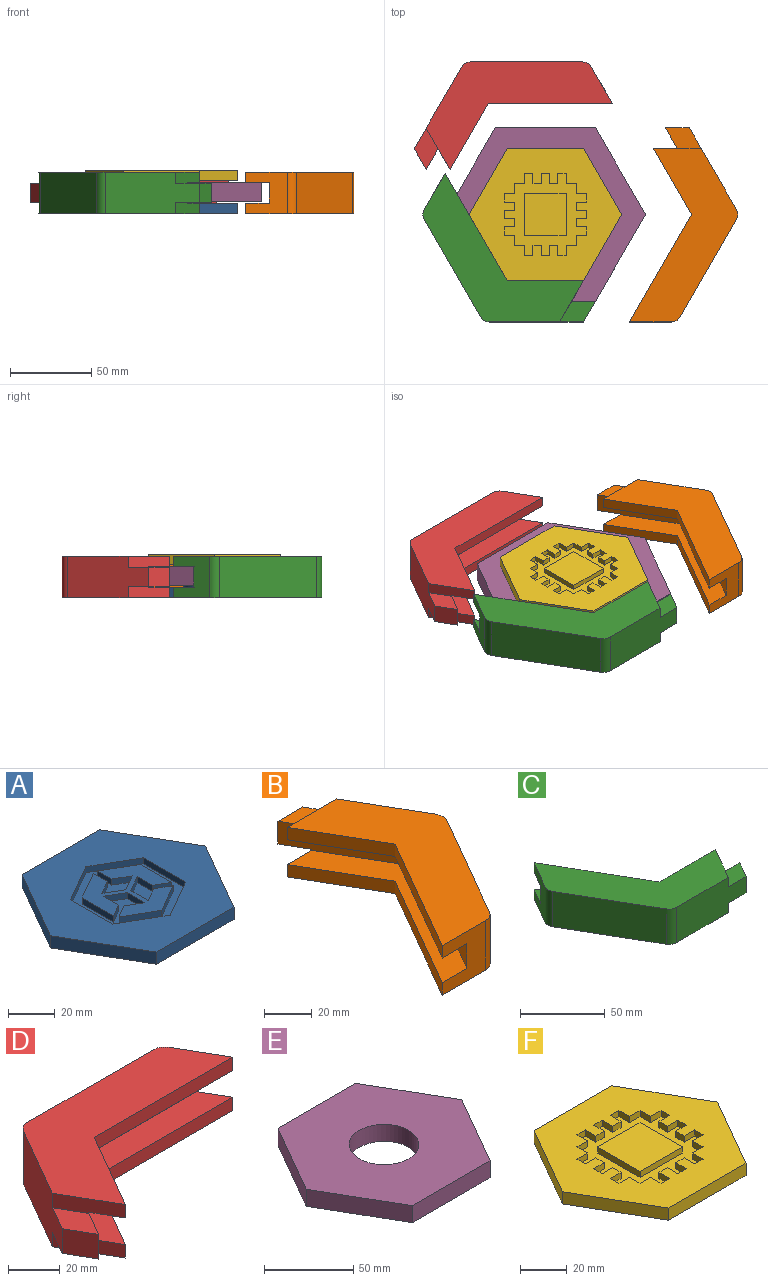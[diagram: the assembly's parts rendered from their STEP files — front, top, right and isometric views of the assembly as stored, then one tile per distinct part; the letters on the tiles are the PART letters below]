
ASSEMBLY  parts=6 mates=5
PART A: 42 faces, bbox 93.7x81.2x12.7 mm
  f0: plane 93.74x81.18mm, normal (0,0,1), area 4031.4mm2, adj f1,f2,f3,f4,f5,f6,f33,f34
  f1: plane 40.59x23.44mm, normal (-0.87,-0.5,0), area 297.6mm2, adj f0,f2,f6,f7
  f2: plane 46.87x6.35mm, normal (0,-1,0), area 297.6mm2, adj f0,f1,f3,f7
  f3: plane 40.59x23.44mm, normal (0.87,-0.5,0), area 297.6mm2, adj f0,f2,f4,f7
  f4: plane 40.59x23.44mm, normal (0.87,0.5,0), area 297.6mm2, adj f0,f3,f5,f7
  f5: plane 46.87x6.35mm, normal (0,1,0), area 297.6mm2, adj f0,f4,f6,f7
  f6: plane 40.59x23.44mm, normal (-0.87,0.5,0), area 297.6mm2, adj f0,f1,f5,f7
  f7: plane 93.74x81.18mm, normal (0,0,-1), area 4567.5mm2, adj f1,f2,f3,f4,f5,f6,f8
  f8: cylinder r=19.05mm len=38.1mm, axis (0,0,1), area 760.1mm2, adj f7,f9
  f9: plane 38.1x38.1mm, normal (0,0,-1), area 1140.1mm2, adj f8
  f10: plane 16.33x9.43mm, normal (-0.5,0.87,0), area 59.9mm2, adj f11,f39,f40,f41
  f11: plane 8.46x3.18mm, normal (1,0,0), area 26.9mm2, adj f10,f12,f40,f41
  f12: plane 7.9x4.56mm, normal (0.5,-0.87,0), area 29mm2, adj f11,f13,f40,f41
  f13: plane 9.17x5.3mm, normal (0.5,0.87,0), area 33.6mm2, adj f12,f14,f40,f41
  f14: plane 9.17x5.3mm, normal (-0.5,0.87,0), area 33.6mm2, adj f13,f15,f40,f41
  f15: plane 7.9x4.56mm, normal (-0.5,-0.87,0), area 29mm2, adj f14,f16,f40,f41
  f16: plane 8.46x3.18mm, normal (-1,0,0), area 26.9mm2, adj f15,f17,f40,f41
  f17: plane 16.33x9.43mm, normal (0.5,0.87,0), area 59.9mm2, adj f16,f18,f40,f41
  f18: plane 18.85x3.18mm, normal (1,0,0), area 59.9mm2, adj f17,f19,f40,f41
  f19: plane 7.33x4.23mm, normal (-0.5,-0.87,0), area 26.9mm2, adj f18,f20,f40,f41
  f20: plane 9.13x3.18mm, normal (-1,0,0), area 29mm2, adj f19,f21,f40,f41
  f21: plane 9.17x5.3mm, normal (0.5,-0.87,0), area 33.6mm2, adj f20,f22,f40,f41
  f22: plane 10.59x3.18mm, normal (1,0,0), area 33.6mm2, adj f21,f23,f40,f41
  f23: plane 7.9x4.56mm, normal (-0.5,0.87,0), area 29mm2, adj f22,f24,f40,f41
  f24: plane 7.33x4.23mm, normal (0.5,0.87,0), area 26.9mm2, adj f23,f25,f40,f41
  f25: plane 16.33x9.43mm, normal (0.5,-0.87,0), area 59.9mm2, adj f24,f26,f40,f41
  f26: plane 16.33x9.43mm, normal (-0.5,-0.87,0), area 59.9mm2, adj f25,f27,f40,f41
  f27: plane 7.33x4.23mm, normal (-0.5,0.87,0), area 26.9mm2, adj f26,f28,f40,f41
  f28: plane 7.9x4.56mm, normal (0.5,0.87,0), area 29mm2, adj f27,f29,f40,f41
  f29: plane 10.59x3.18mm, normal (-1,0,0), area 33.6mm2, adj f28,f30,f40,f41
  f30: plane 9.17x5.3mm, normal (-0.5,-0.87,0), area 33.6mm2, adj f29,f31,f40,f41
  f31: plane 9.13x3.18mm, normal (1,0,0), area 29mm2, adj f30,f32,f40,f41
  f32: plane 7.33x4.23mm, normal (0.5,-0.87,0), area 26.9mm2, adj f31,f39,f40,f41
  f33: plane 22x12.7mm, normal (0.5,0.87,0), area 80.6mm2, adj f0,f34,f38,f40
  f34: plane 22x12.7mm, normal (-0.5,0.87,0), area 80.6mm2, adj f0,f33,f35,f40
  f35: plane 25.4x3.18mm, normal (-1,0,0), area 80.6mm2, adj f0,f34,f36,f40
  f36: plane 22x12.7mm, normal (-0.5,-0.87,0), area 80.6mm2, adj f0,f35,f37,f40
  f37: plane 22x12.7mm, normal (0.5,-0.87,0), area 80.6mm2, adj f0,f36,f38,f40
  f38: plane 25.4x3.18mm, normal (1,0,0), area 80.6mm2, adj f0,f33,f37,f40
  f39: plane 18.85x3.18mm, normal (-1,0,0), area 59.9mm2, adj f10,f32,f40,f41
  f40: plane 50.8x43.99mm, normal (0,0,1), area 959.3mm2, adj f10,f11,f12,f13,f14,f15,f16,f17
  f41: plane 39.91x35.2mm, normal (0,0,1), area 716.8mm2, adj f10,f11,f12,f13,f14,f15,f16,f17
PART B: 20 faces, bbox 66.4x119.3x25.4 mm
  f0: plane 29.33x6.86mm, normal (0,1,0), area 193.7mm2, adj f1,f3,f5,f14,f16,f18
  f1: plane 40.59x23.44mm, normal (-0.87,-0.5,0), area 297.6mm2, adj f0,f2,f14,f18
  f2: plane 65.99x38.1mm, normal (-0.87,0.5,0), area 483.9mm2, adj f1,f9,f14,f18
  f3: plane 50.12x28.93mm, normal (0.87,0.5,0), area 1268.7mm2, adj f0,f4,f6,f12,f13,f14,f15,f16
  f4: plane 14.66x11.68mm, normal (0,1,0), area 171.3mm2, adj f3,f5,f15,f16
  f5: plane 53.29x30.77mm, normal (-0.87,-0.5,0), area 766.6mm2, adj f0,f4,f6,f15,f16,f17,f18,f19
  f6: plane 29.33x6.86mm, normal (0,1,0), area 193.7mm2, adj f3,f5,f7,f13,f15,f19
  f7: plane 40.59x23.44mm, normal (-0.87,-0.5,0), area 297.6mm2, adj f6,f8,f13,f19
  f8: plane 65.99x38.1mm, normal (-0.87,0.5,0), area 483.9mm2, adj f7,f9,f13,f19
  f9: plane 25.66x25.4mm, normal (0,-1,0), area 465.6mm2, adj f2,f8,f10,f13,f14,f17,f18,f19
  f10: cylinder r=6.35mm len=25.4mm, axis (0,0,-1), area 168.9mm2, adj f9,f11,f13,f14
  f11: plane 59.64x34.43mm, normal (0.87,-0.5,0), area 1749.2mm2, adj f10,f12,f13,f14
  f12: cylinder r=6.35mm len=25.4mm, axis (0,0,-1), area 168.9mm2, adj f3,f11,f13,f14
  f13: plane 106.58x66.45mm, normal (0,0,1), area 3121.7mm2, adj f3,f6,f7,f8,f9,f10,f11,f12
  f14: plane 106.58x66.45mm, normal (0,0,-1), area 3121.7mm2, adj f0,f1,f2,f3,f9,f10,f11,f12
  f15: plane 22x12.7mm, normal (0,0,1), area 186.2mm2, adj f3,f4,f5,f6
  f16: plane 22x12.7mm, normal (0,0,-1), area 186.2mm2, adj f0,f3,f4,f5
  f17: plane 65.99x38.1mm, normal (-0.87,0.5,0), area 967.7mm2, adj f5,f9,f18,f19
  f18: plane 106.58x52.76mm, normal (0,0,1), area 1563mm2, adj f0,f1,f2,f5,f9,f17
  f19: plane 106.58x52.76mm, normal (0,0,-1), area 1563mm2, adj f5,f6,f7,f8,f9,f17
PART C: 20 faces, bbox 106x91.4x25.4 mm
  f0: plane 25.4x14.66mm, normal (0.87,-0.5,0), area 193.7mm2, adj f1,f3,f5,f14,f16,f18
  f1: plane 46.87x6.35mm, normal (0,1,0), area 297.6mm2, adj f0,f2,f14,f18
  f2: plane 65.99x38.1mm, normal (0.87,0.5,0), area 483.9mm2, adj f1,f9,f14,f18
  f3: plane 57.87x25.4mm, normal (0,-1,0), area 1268.7mm2, adj f0,f4,f6,f12,f13,f14,f15,f16
  f4: plane 12.7x11.68mm, normal (0.87,-0.5,0), area 171.3mm2, adj f3,f5,f15,f16
  f5: plane 61.54x12.7mm, normal (0,1,0), area 766.6mm2, adj f0,f4,f6,f15,f16,f17,f18,f19
  f6: plane 25.4x14.66mm, normal (0.87,-0.5,0), area 193.7mm2, adj f3,f5,f7,f13,f15,f19
  f7: plane 46.87x6.35mm, normal (0,1,0), area 297.6mm2, adj f6,f8,f13,f19
  f8: plane 65.99x38.1mm, normal (0.87,0.5,0), area 483.9mm2, adj f7,f9,f13,f19
  f9: plane 25.4x22.23mm, normal (-0.87,0.5,0), area 465.6mm2, adj f2,f8,f10,f13,f14,f17,f18,f19
  f10: cylinder r=6.35mm len=25.4mm, axis (0,0,-1), area 168.9mm2, adj f9,f11,f13,f14
  f11: plane 59.64x34.43mm, normal (-0.87,-0.5,0), area 1749.2mm2, adj f10,f12,f13,f14
  f12: cylinder r=6.35mm len=25.4mm, axis (0,0,-1), area 168.9mm2, adj f3,f11,f13,f14
  f13: plane 98.65x91.39mm, normal (0,0,1), area 3121.7mm2, adj f3,f6,f7,f8,f9,f10,f11,f12
  f14: plane 98.65x91.39mm, normal (0,0,-1), area 3121.7mm2, adj f0,f1,f2,f3,f9,f10,f11,f12
  f15: plane 22x12.7mm, normal (0,0,1), area 186.2mm2, adj f3,f4,f5,f6
  f16: plane 22x12.7mm, normal (0,0,-1), area 186.2mm2, adj f0,f3,f4,f5
  f17: plane 65.99x38.1mm, normal (0.87,0.5,0), area 967.7mm2, adj f5,f9,f18,f19
  f18: plane 92.3x78.69mm, normal (0,0,1), area 1563mm2, adj f0,f1,f2,f5,f9,f17
  f19: plane 92.3x78.69mm, normal (0,0,-1), area 1563mm2, adj f5,f6,f7,f8,f9,f17
PART D: 20 faces, bbox 121.6x66x25.4 mm
  f0: plane 25.4x14.66mm, normal (-0.87,-0.5,0), area 193.7mm2, adj f1,f3,f5,f14,f16,f18
  f1: plane 40.59x23.44mm, normal (0.87,-0.5,0), area 297.6mm2, adj f0,f2,f14,f18
  f2: plane 76.2x6.35mm, normal (0,-1,0), area 483.9mm2, adj f1,f9,f14,f18
  f3: plane 50.12x28.93mm, normal (-0.87,0.5,0), area 1268.7mm2, adj f0,f4,f6,f12,f13,f14,f15,f16
  f4: plane 12.7x11.68mm, normal (-0.87,-0.5,0), area 171.3mm2, adj f3,f5,f15,f16
  f5: plane 53.29x30.77mm, normal (0.87,-0.5,0), area 766.6mm2, adj f0,f4,f6,f15,f16,f17,f18,f19
  f6: plane 25.4x14.66mm, normal (-0.87,-0.5,0), area 193.7mm2, adj f3,f5,f7,f13,f15,f19
  f7: plane 40.59x23.44mm, normal (0.87,-0.5,0), area 297.6mm2, adj f6,f8,f13,f19
  f8: plane 76.2x6.35mm, normal (0,-1,0), area 483.9mm2, adj f7,f9,f13,f19
  f9: plane 25.4x22.23mm, normal (0.87,0.5,0), area 465.6mm2, adj f2,f8,f10,f13,f14,f17,f18,f19
  f10: cylinder r=6.35mm len=25.4mm, axis (0,0,-1), area 168.9mm2, adj f9,f11,f13,f14
  f11: plane 68.87x25.4mm, normal (0,1,0), area 1749.2mm2, adj f10,f12,f13,f14
  f12: cylinder r=6.35mm len=25.4mm, axis (0,0,-1), area 168.9mm2, adj f3,f11,f13,f14
  f13: plane 114.3x65.99mm, normal (0,0,1), area 3121.7mm2, adj f3,f6,f7,f8,f9,f10,f11,f12
  f14: plane 114.3x65.99mm, normal (0,0,-1), area 3121.7mm2, adj f0,f1,f2,f3,f9,f10,f11,f12
  f15: plane 25.4x14.66mm, normal (0,0,1), area 186.2mm2, adj f3,f4,f5,f6
  f16: plane 25.4x14.66mm, normal (0,0,-1), area 186.2mm2, adj f0,f3,f4,f5
  f17: plane 76.2x12.7mm, normal (0,-1,0), area 967.7mm2, adj f5,f9,f18,f19
  f18: plane 106.97x53.29mm, normal (0,0,1), area 1563mm2, adj f0,f1,f2,f5,f9,f17
  f19: plane 106.97x53.29mm, normal (0,0,-1), area 1563mm2, adj f5,f6,f7,f8,f9,f17
PART E: 9 faces, bbox 123.1x106.6x11.7 mm
  f0: plane 53.29x30.77mm, normal (-0.87,-0.5,0), area 719mm2, adj f1,f5,f6,f7
  f1: plane 61.54x11.68mm, normal (0,-1,0), area 719mm2, adj f0,f2,f6,f7
  f2: plane 53.29x30.77mm, normal (0.87,-0.5,0), area 719mm2, adj f1,f3,f6,f7
  f3: plane 53.29x30.77mm, normal (0.87,0.5,0), area 719mm2, adj f2,f4,f6,f7
  f4: plane 61.54x11.68mm, normal (0,1,0), area 719mm2, adj f3,f5,f6,f7
  f5: plane 53.29x30.77mm, normal (-0.87,0.5,0), area 719mm2, adj f0,f4,f6,f7
  f6: plane 123.07x106.58mm, normal (0,0,1), area 8636.2mm2, adj f0,f1,f2,f3,f4,f5,f8
  f7: plane 123.07x106.58mm, normal (0,0,-1), area 8636.2mm2, adj f0,f1,f2,f3,f4,f5,f8
  f8: cylinder r=19.56mm len=39.12mm, axis (0,0,1), area 1435.8mm2, adj f6,f7
PART F: 68 faces, bbox 93.7x81.2x12.7 mm
  f0: plane 93.74x81.18mm, normal (0,0,1), area 3868.9mm2, adj f1,f2,f3,f4,f5,f6,f13,f14
  f1: plane 40.59x23.44mm, normal (-0.87,-0.5,0), area 297.6mm2, adj f0,f2,f6,f7
  f2: plane 46.87x6.35mm, normal (0,-1,0), area 297.6mm2, adj f0,f1,f3,f7
  f3: plane 40.59x23.44mm, normal (0.87,-0.5,0), area 297.6mm2, adj f0,f2,f4,f7
  f4: plane 40.59x23.44mm, normal (0.87,0.5,0), area 297.6mm2, adj f0,f3,f5,f7
  f5: plane 46.87x6.35mm, normal (0,1,0), area 297.6mm2, adj f0,f4,f6,f7
  f6: plane 40.59x23.44mm, normal (-0.87,0.5,0), area 297.6mm2, adj f0,f1,f5,f7
  f7: plane 93.74x81.18mm, normal (0,0,-1), area 4567.5mm2, adj f1,f2,f3,f4,f5,f6,f8
  f8: cylinder r=19.05mm len=38.1mm, axis (0,0,1), area 760.1mm2, adj f7,f9
  f9: plane 38.1x38.1mm, normal (0,0,-1), area 1140.1mm2, adj f8
  f10: plane 25.4x3.18mm, normal (0,1,0), area 80.6mm2, adj f11,f65,f66,f67
  f11: plane 25.4x3.18mm, normal (1,0,0), area 80.6mm2, adj f10,f12,f66,f67
  f12: plane 25.4x3.18mm, normal (0,-1,0), area 80.6mm2, adj f11,f65,f66,f67
  f13: plane 5.08x3.18mm, normal (0,1,0), area 16.1mm2, adj f0,f14,f64,f66
  f14: plane 6.35x3.18mm, normal (-1,0,0), area 20.2mm2, adj f0,f13,f15,f66
  f15: plane 6.35x3.18mm, normal (0,1,0), area 20.2mm2, adj f0,f14,f16,f66
  f16: plane 6.35x3.18mm, normal (-1,0,0), area 20.2mm2, adj f0,f15,f17,f66
  f17: plane 6.35x3.18mm, normal (0,1,0), area 20.2mm2, adj f0,f16,f18,f66
  f18: plane 5.08x3.18mm, normal (-1,0,0), area 16.1mm2, adj f0,f17,f19,f66
  f19: plane 6.35x3.18mm, normal (0,-1,0), area 20.2mm2, adj f0,f18,f20,f66
  f20: plane 5.08x3.18mm, normal (-1,0,0), area 16.1mm2, adj f0,f19,f21,f66
  f21: plane 6.35x3.18mm, normal (0,1,0), area 20.2mm2, adj f0,f20,f22,f66
  f22: plane 5.08x3.18mm, normal (-1,0,0), area 16.1mm2, adj f0,f21,f23,f66
  f23: plane 6.35x3.18mm, normal (0,-1,0), area 20.2mm2, adj f0,f22,f24,f66
  f24: plane 5.08x3.18mm, normal (-1,0,0), area 16.1mm2, adj f0,f23,f25,f66
  f25: plane 6.35x3.18mm, normal (0,1,0), area 20.2mm2, adj f0,f24,f26,f66
  f26: plane 5.08x3.18mm, normal (-1,0,0), area 16.1mm2, adj f0,f25,f27,f66
  f27: plane 6.35x3.18mm, normal (0,-1,0), area 20.2mm2, adj f0,f26,f28,f66
  f28: plane 6.35x3.18mm, normal (-1,0,0), area 20.2mm2, adj f0,f27,f29,f66
  f29: plane 6.35x3.18mm, normal (0,-1,0), area 20.2mm2, adj f0,f28,f30,f66
  f30: plane 6.35x3.18mm, normal (-1,0,0), area 20.2mm2, adj f0,f29,f31,f66
  f31: plane 5.08x3.18mm, normal (0,-1,0), area 16.1mm2, adj f0,f30,f32,f66
  f32: plane 6.35x3.18mm, normal (1,0,0), area 20.2mm2, adj f0,f31,f33,f66
  f33: plane 5.08x3.18mm, normal (0,-1,0), area 16.1mm2, adj f0,f32,f34,f66
  f34: plane 6.35x3.18mm, normal (-1,0,0), area 20.2mm2, adj f0,f33,f35,f66
  f35: plane 5.08x3.18mm, normal (0,-1,0), area 16.1mm2, adj f0,f34,f36,f66
  f36: plane 6.35x3.18mm, normal (1,0,0), area 20.2mm2, adj f0,f35,f37,f66
  f37: plane 5.08x3.18mm, normal (0,-1,0), area 16.1mm2, adj f0,f36,f38,f66
  f38: plane 6.35x3.18mm, normal (-1,0,0), area 20.2mm2, adj f0,f37,f39,f66
  f39: plane 5.08x3.18mm, normal (0,-1,0), area 16.1mm2, adj f0,f38,f40,f66
  f40: plane 6.35x3.18mm, normal (1,0,0), area 20.2mm2, adj f0,f39,f41,f66
  f41: plane 6.35x3.18mm, normal (0,-1,0), area 20.2mm2, adj f0,f40,f42,f66
  f42: plane 6.35x3.18mm, normal (1,0,0), area 20.2mm2, adj f0,f41,f43,f66
  f43: plane 6.35x3.18mm, normal (0,-1,0), area 20.2mm2, adj f0,f42,f44,f66
  f44: plane 5.08x3.18mm, normal (1,0,0), area 16.1mm2, adj f0,f43,f45,f66
  f45: plane 6.35x3.18mm, normal (0,1,0), area 20.2mm2, adj f0,f44,f46,f66
  f46: plane 5.08x3.18mm, normal (1,0,0), area 16.1mm2, adj f0,f45,f47,f66
  f47: plane 6.35x3.18mm, normal (0,-1,0), area 20.2mm2, adj f0,f46,f48,f66
  f48: plane 5.08x3.18mm, normal (1,0,0), area 16.1mm2, adj f0,f47,f49,f66
  f49: plane 6.35x3.18mm, normal (0,1,0), area 20.2mm2, adj f0,f48,f50,f66
  f50: plane 5.08x3.18mm, normal (1,0,0), area 16.1mm2, adj f0,f49,f51,f66
  f51: plane 6.35x3.18mm, normal (0,-1,0), area 20.2mm2, adj f0,f50,f52,f66
  f52: plane 5.08x3.18mm, normal (1,0,0), area 16.1mm2, adj f0,f51,f53,f66
  f53: plane 6.35x3.18mm, normal (0,1,0), area 20.2mm2, adj f0,f52,f54,f66
  f54: plane 6.35x3.18mm, normal (1,0,0), area 20.2mm2, adj f0,f53,f55,f66
  f55: plane 6.35x3.18mm, normal (0,1,0), area 20.2mm2, adj f0,f54,f56,f66
  f56: plane 6.35x3.18mm, normal (1,0,0), area 20.2mm2, adj f0,f55,f57,f66
  f57: plane 5.08x3.18mm, normal (0,1,0), area 16.1mm2, adj f0,f56,f58,f66
  f58: plane 6.35x3.18mm, normal (-1,0,0), area 20.2mm2, adj f0,f57,f59,f66
  f59: plane 5.08x3.18mm, normal (0,1,0), area 16.1mm2, adj f0,f58,f60,f66
  f60: plane 6.35x3.18mm, normal (1,0,0), area 20.2mm2, adj f0,f59,f61,f66
  f61: plane 5.08x3.18mm, normal (0,1,0), area 16.1mm2, adj f0,f60,f62,f66
  f62: plane 6.35x3.18mm, normal (-1,0,0), area 20.2mm2, adj f0,f61,f63,f66
  f63: plane 5.08x3.18mm, normal (0,1,0), area 16.1mm2, adj f0,f62,f64,f66
  f64: plane 6.35x3.18mm, normal (1,0,0), area 20.2mm2, adj f0,f13,f63,f66
  f65: plane 25.4x3.18mm, normal (-1,0,0), area 80.6mm2, adj f10,f12,f66,f67
  f66: plane 50.8x50.8mm, normal (0,0,1), area 1193.5mm2, adj f10,f11,f12,f13,f14,f15,f16,f17
  f67: plane 25.4x25.4mm, normal (0,0,1), area 645.2mm2, adj f10,f11,f12,f65
PLACE A rot(axis=(1,0,0),180deg) t=(0,0,49.53)mm
PLACE B t=(42.89,0,-0.51)mm
PLACE C t=(0,0,-0.51)mm
PLACE D t=(-11.64,27.62,-0.51)mm
PLACE E at identity fixed
PLACE F t=(0,0,1.27)mm
MATE slider A.f8 <-> E.f8  axis (0,0,1) through (0,0,-0.76)mm
MATE planar E.f6 <-> C.f19  axis (0,0,1) through (-30.77,-53.29,5.84)mm
MATE planar E.f6 <-> D.f19  axis (0,0,1) through (-30.77,53.29,5.84)mm
MATE slider F.f8 <-> E.f8  axis (0,0,-1) through (0,0,0.76)mm
MATE planar B.f19 <-> E.f6  axis (0,0,-1) through (104.43,0,5.84)mm
